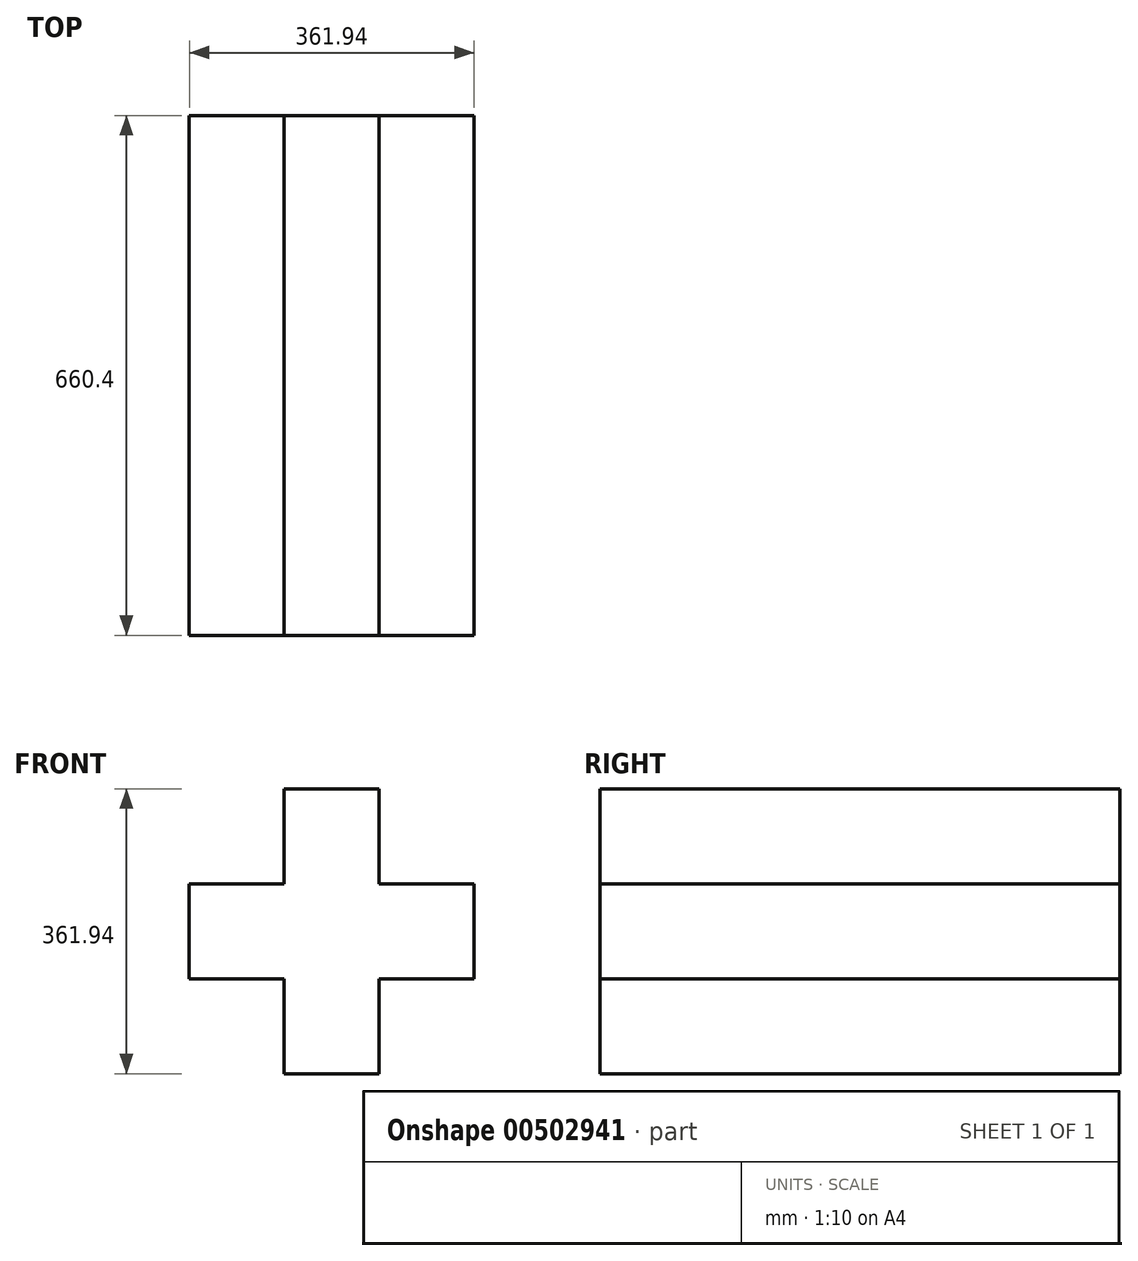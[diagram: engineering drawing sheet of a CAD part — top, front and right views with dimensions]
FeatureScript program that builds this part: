
annotation { "Feature Type Name" : "Feature", "Feature Type Description" : "" }
export const myFeature = defineFeature(function(context is Context, id is Id, definition is map)
    precondition{}
    {
        {
            var Q0;
            Q0=qCreatedBy(makeId("Front.planeOp"),FACE);
            var sketch = newSketch(context, id + "F0", { "sketchPlane" : qUnion([Q0])});
            skLineSegment(sketch, "E0.top", {"start": v(60.33, 180.97) * mm, "end": v(-60.33, 180.97) * mm});
            skLineSegment(sketch, "E0.left", {"start": v(60.33, 60.33) * mm, "end": v(60.33, 180.97) * mm});
            skLineSegment(sketch, "E0.right", {"start": v(-60.33, 60.33) * mm, "end": v(-60.33, 180.97) * mm});
            skPoint(sketch, "E0.middle", {"position": v(0, 120.65) * mm});
            skPoint(sketch, "E1.middle", {"position": v(0, 0) * mm});
            skLineSegment(sketch, "E2.MirrorCS", {"start": v(60.33, -180.97) * mm, "end": v(-60.33, -180.97) * mm});
            skLineSegment(sketch, "E3.MirrorCS", {"start": v(-60.33, -60.33) * mm, "end": v(-60.33, -180.97) * mm});
            skLineSegment(sketch, "E4.MirrorCS", {"start": v(60.33, -60.33) * mm, "end": v(60.33, -180.97) * mm});
            skLineSegment(sketch, "E5.bottom", {"start": v(-60.32, -60.33) * mm, "end": v(-180.98, -60.33) * mm});
            skLineSegment(sketch, "E5.top", {"start": v(-60.32, 60.32) * mm, "end": v(-180.98, 60.32) * mm});
            skLineSegment(sketch, "E5.right", {"start": v(-180.98, -60.32) * mm, "end": v(-180.98, 60.33) * mm});
            skPoint(sketch, "E5.middle", {"position": v(-120.65, 0) * mm});
            skLineSegment(sketch, "E6.MirrorCS", {"start": v(180.98, -60.32) * mm, "end": v(180.98, 60.33) * mm});
            skLineSegment(sketch, "E7.MirrorCS", {"start": v(60.32, 60.32) * mm, "end": v(180.98, 60.32) * mm});
            skLineSegment(sketch, "E8.MirrorCS", {"start": v(60.32, -60.33) * mm, "end": v(180.98, -60.33) * mm});
            skPoint(sketch, "E1.right.start.orphan", {"position": v(60.33, 60.33) * mm});
            skPoint(sketch, "E1.top.end.orphan", {"position": v(60.32, -60.33) * mm});
            skSolve(sketch);
        }
        {
            var Q0;
            Q0=makeQuery(id+"F0.imprint","IMPRINT",FACE,{"disambiguationData":[TD([[makeQuery(id+"F0.imprint","IMPRINT",EDGE,{"derivedFrom":sQuery(id+"F0.wireOp",EDGE,"E0.top")}),1.0]])]});
            extrude(context, id + "F1", {"entities" : qUnion([Q0]), "depth" : 660.4 * mm});
        }
    });
